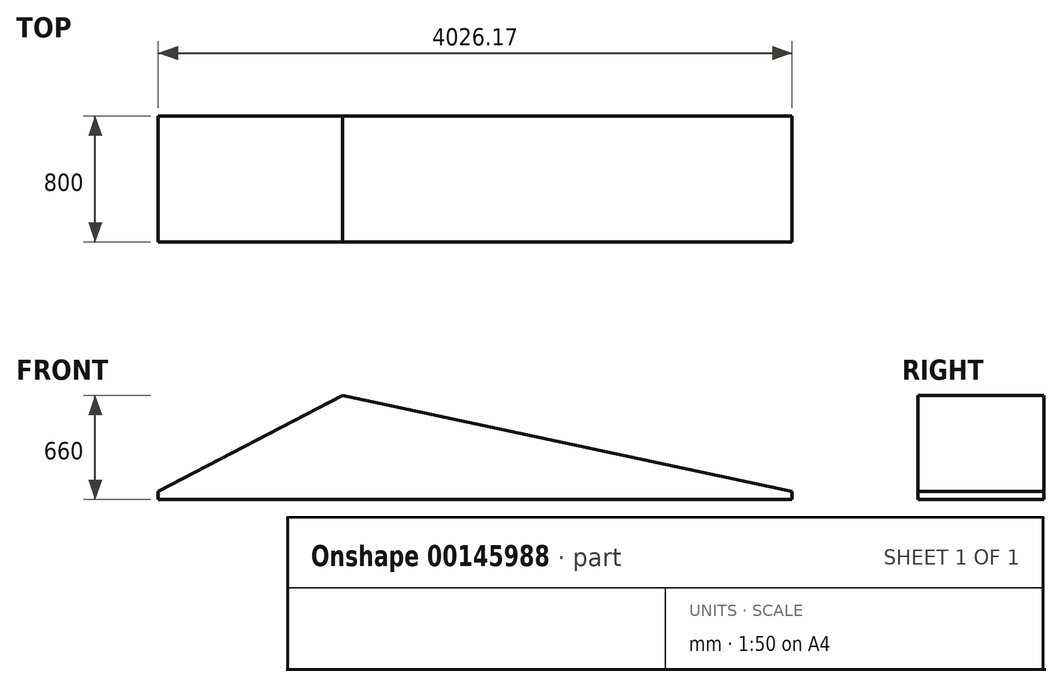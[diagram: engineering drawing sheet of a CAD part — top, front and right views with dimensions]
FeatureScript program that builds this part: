
annotation { "Feature Type Name" : "Feature", "Feature Type Description" : "" }
export const myFeature = defineFeature(function(context is Context, id is Id, definition is map)
    precondition{}
    {
        {
            var Q0;
            Q0=qCreatedBy(makeId("Front.planeOp"),FACE);
            var sketch = newSketch(context, id + "F0", { "sketchPlane" : qUnion([Q0])});
            skLineSegment(sketch, "E0", {"start": v(-1664.3, 0) * mm, "end": v(-493.7, 610) * mm});
            skLineSegment(sketch, "E1", {"start": v(-493.7, 610) * mm, "end": v(2361.88, 0) * mm});
            skLineSegment(sketch, "E2", {"start": v(-1664.3, 0) * mm, "end": v(-1664.3, -50) * mm});
            skLineSegment(sketch, "E3", {"start": v(2361.88, 0) * mm, "end": v(2361.88, -50) * mm});
            skLineSegment(sketch, "E4", {"start": v(-1664.3, -50) * mm, "end": v(2361.88, -50) * mm});
            skLineSegment(sketch, "E5", {"start": v(-493.7, 610) * mm, "end": v(-493.7, -50) * mm});
            skSolve(sketch);
        }
        {
            var Q0;
            Q0=makeQuery(id+"F0.imprint","IMPRINT",FACE,{"disambiguationData":[TD([[makeQuery(id+"F0.imprint","IMPRINT",EDGE,{"derivedFrom":sQuery(id+"F0.wireOp",EDGE,"E0")}),-1.0]])]});
            var Q1;
            Q1=makeQuery(id+"F0.imprint","IMPRINT",FACE,{"disambiguationData":[TD([[makeQuery(id+"F0.imprint","IMPRINT",EDGE,{"derivedFrom":sQuery(id+"F0.wireOp",EDGE,"E1")}),-1.0]])]});
            extrude(context, id + "F1", {"entities" : qUnion([Q0, Q1]), "depth" : 800 * mm});
        }
    });
